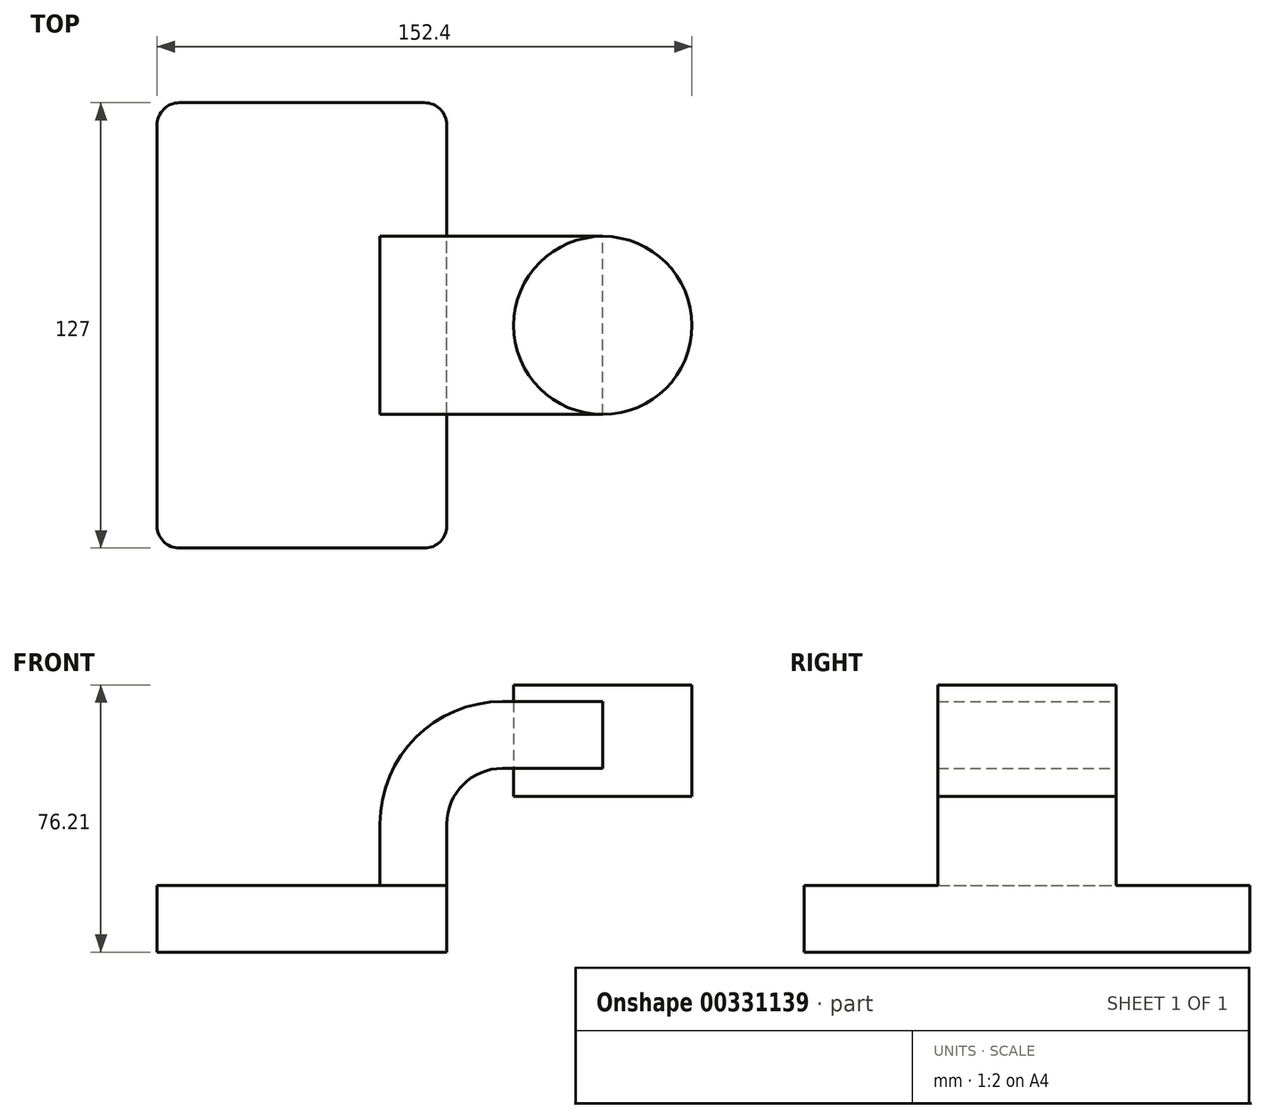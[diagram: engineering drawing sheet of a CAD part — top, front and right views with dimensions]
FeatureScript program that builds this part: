
annotation { "Feature Type Name" : "Feature", "Feature Type Description" : "" }
export const myFeature = defineFeature(function(context is Context, id is Id, definition is map)
    precondition{}
    {
        {
            var Q0;
            Q0=qCreatedBy(makeId("Front.planeOp"),FACE);
            var sketch = newSketch(context, id + "F0", { "sketchPlane" : qUnion([Q0])});
            skLineSegment(sketch, "E0.bottom", {"start": v(41.28, -9.52) * mm, "end": v(-41.27, -9.53) * mm});
            skLineSegment(sketch, "E0.top", {"start": v(41.28, 9.53) * mm, "end": v(-41.28, 9.53) * mm});
            skLineSegment(sketch, "E0.left", {"start": v(41.28, -9.52) * mm, "end": v(41.28, 9.53) * mm});
            skLineSegment(sketch, "E0.right", {"start": v(-41.27, -9.52) * mm, "end": v(-41.28, 9.53) * mm});
            skPoint(sketch, "E0.middle", {"position": v(0, 0) * mm});
            skLineSegment(sketch, "E1.bottom", {"start": v(60.32, 34.93) * mm, "end": v(111.12, 34.93) * mm});
            skLineSegment(sketch, "E1.top", {"start": v(60.32, 66.68) * mm, "end": v(111.12, 66.68) * mm});
            skLineSegment(sketch, "E1.left", {"start": v(60.32, 34.93) * mm, "end": v(60.32, 66.68) * mm});
            skLineSegment(sketch, "E1.right", {"start": v(111.12, 34.93) * mm, "end": v(111.12, 66.68) * mm});
            skPoint(sketch, "E1.middle", {"position": v(85.72, 50.8) * mm});
            skLineSegment(sketch, "E2", {"start": v(41.28, 9.53) * mm, "end": v(41.28, 27) * mm});
            skArc(sketch, "E3", {"start": v(41.28, 27) * mm, "mid": v(45.92, 38.23) * mm, "end": v(57.15, 42.88) * mm});
            skLineSegment(sketch, "E4", {"start": v(57.15, 42.88) * mm, "end": v(85.73, 42.88) * mm});
            skLineSegment(sketch, "E5.0", {"start": v(57.15, 61.93) * mm, "end": v(85.73, 61.93) * mm});
            skArc(sketch, "E5.1", {"start": v(22.23, 27) * mm, "mid": v(32.45, 51.7) * mm, "end": v(57.15, 61.93) * mm});
            skLineSegment(sketch, "E5.2", {"start": v(22.22, 9.53) * mm, "end": v(22.22, 27) * mm});
            skLineSegment(sketch, "E6", {"start": v(85.72, 34.93) * mm, "end": v(85.72, 66.68) * mm});
            skFitSpline(sketch, "E7", {"points": [v(-41.28, 9.53) * mm, v(57.15, 61.93) * mm], "startDerivative": vector(0.57, 105.52) * mm, "endDerivative": vector(147.28, -1.73) * mm});
            skSolve(sketch);
        }
        {
            var Q0;
            Q0=makeQuery(id+"F0.imprint","IMPRINT",FACE,{"disambiguationData":[TD([[makeQuery(id+"F0.imprint","IMPRINT",EDGE,{"derivedFrom":sQuery(id+"F0.wireOp",EDGE,"E0.bottom")}),-1.0]])]});
            extrude(context, id + "F1", {"entities" : qUnion([Q0]), "endBound" : BoundingType.SYMMETRIC, "depth" : 127 * mm});
        }
        {
            var Q0;
            {var subQ1=sQuery(id+"F0.wireOp",EDGE,"E2");Q0=makeQuery(id+"F0.imprint","IMPRINT",FACE,{"disambiguationData":[TD([[makeQuery(id+"F0.imprint","IMPRINT",EDGE,{"derivedFrom":subQ1}),1.0]])]});}
            var Q1;
            {var subQ0=sQuery(id+"F0.wireOp",EDGE,"E4");var subQ1=sQuery(id+"F0.wireOp",EDGE,"E1.left");var subQ2=makeQuery(id+"F0.imprint","INTERSECT",VERTEX,{"derivedFrom":[subQ1,subQ0]});Q1=makeQuery(id+"F0.imprint","IMPRINT",FACE,{"disambiguationData":[TD([[makeQuery(id+"F0.imprint","IMPRINT",EDGE,{"disambiguationData":[TD([[subQ2,-1.0]])],"derivedFrom":subQ1}),-1.0]])]});}
            extrude(context, id + "F2", {"entities" : qUnion([Q0, Q1]), "operationType" : NewBodyOperationType.ADD, "endBound" : BoundingType.SYMMETRIC, "depth" : 50.8 * mm});
        }
        {
            var Q0;
            Q0=makeQuery(id+"F0.imprint","IMPRINT",FACE,{"disambiguationData":[TD([[makeQuery(id+"F0.imprint","IMPRINT",EDGE,{"derivedFrom":sQuery(id+"F0.wireOp",EDGE,"E5.1")}),1.0]])]});
            extrude(context, id + "F3", {"entities" : qUnion([Q0]), "operationType" : NewBodyOperationType.ADD, "endBound" : BoundingType.SYMMETRIC, "depth" : 15.88 * mm});
        }
        {
            var Q0;
            {var subQ0=sQuery(id+"F0.wireOp",EDGE,"E1.right");Q0=makeQuery(id+"F0.imprint","IMPRINT",FACE,{"disambiguationData":[TD([[makeQuery(id+"F0.imprint","IMPRINT",EDGE,{"derivedFrom":subQ0}),1.0]])]});}
            var Q1;
            Q1=sQuery(id+"F0.wireOp",EDGE,"E6");
            revolve(context, id + "F4", {"entities" : qUnion([Q0]), "axis" : qUnion([Q1]), "revolveType" : RevolveType.FULL});
        }
        {
            var Q0;
            Q0=makeQuery(id+"F1.opExtrude","CAP_EDGE",EDGE,{"disambiguationData":[OSD([sQuery(id+"F0.wireOp",EDGE,"E0.right")])],"isStart":false});
            var Q1;
            Q1=makeQuery(id+"F1.opExtrude","CAP_EDGE",EDGE,{"disambiguationData":[OSD([sQuery(id+"F0.wireOp",EDGE,"E0.left")])],"isStart":false});
            var Q2;
            Q2=makeQuery(id+"F1.opExtrude","CAP_EDGE",EDGE,{"disambiguationData":[OSD([sQuery(id+"F0.wireOp",EDGE,"E0.left")])],"isStart":true});
            var Q3;
            Q3=makeQuery(id+"F1.opExtrude","CAP_EDGE",EDGE,{"disambiguationData":[OSD([sQuery(id+"F0.wireOp",EDGE,"E0.right")])],"isStart":true});
            fillet(context, id + "F5", {"entities" : qUnion([Q0, Q1, Q2, Q3]), "radius" : 6.35 * mm, "tangentPropagation" : true, "allowEdgeOverflow" : false});
        }
    });
